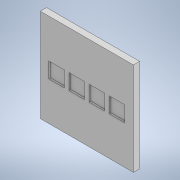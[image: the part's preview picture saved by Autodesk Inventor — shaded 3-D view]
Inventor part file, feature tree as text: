
AUTODESK INVENTOR PART (.ipt)
format: ipt  version: 2022.5 (Build 265521000, 521)  size: 127,488 bytes
history: native  units: mm
features: extrude x2, sketch x2, other x1, projected_geometry x1
ambient origin geometry x8: Origin, YZ Plane, XZ Plane, XY Plane, X Axis, Y Axis, Z Axis, Center Point
bodies: Body1 (feature_tree)
feature tree (6):
  other  "Sólido1"
  extrude  "Extrusión1"  Depth=300.0mm
  extrude  "Extrusión2"  Depth=50.0mm
  sketch  "Boceto1"  dims[d0=300.0mm d1=300.0mm]
  sketch  "Boceto2"  dims[d2=20.0mm d3=0.0mm d4=50.0mm d5=50.0mm d6=15.0mm d7=125.0mm d8=20.0mm d10=65.0mm d11=10.0mm d13=10.0mm d15=300.0mm d16=5.0mm d17=0.0mm]
  projected_geometry  "Contorno proyectado1"
